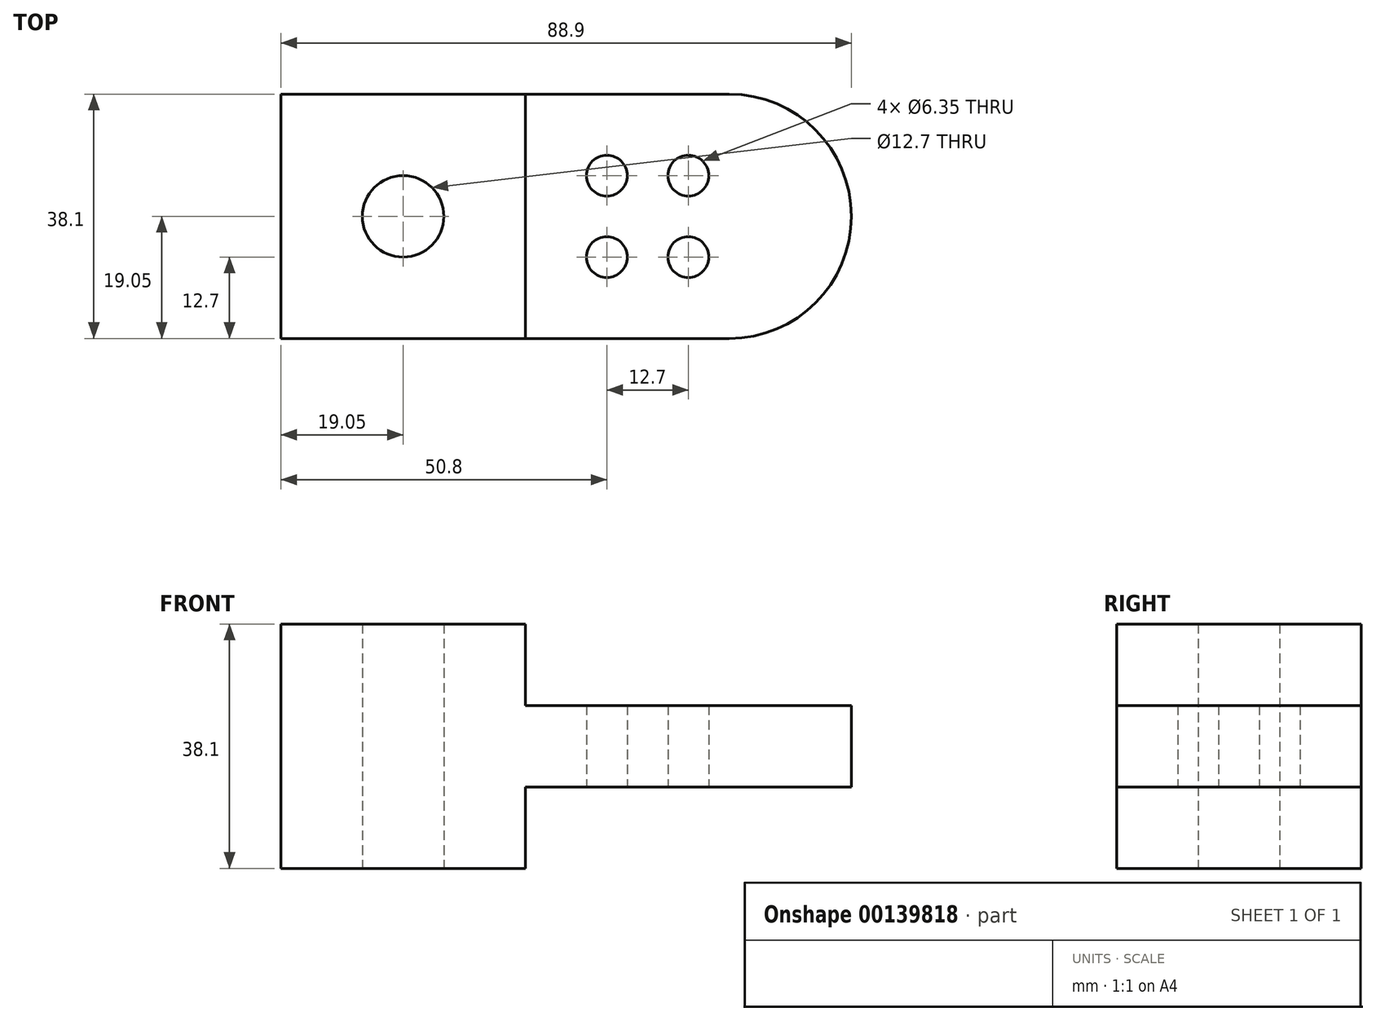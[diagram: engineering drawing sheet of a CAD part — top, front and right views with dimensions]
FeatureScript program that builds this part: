
annotation { "Feature Type Name" : "Feature", "Feature Type Description" : "" }
export const myFeature = defineFeature(function(context is Context, id is Id, definition is map)
    precondition{}
    {
        {
            var Q0;
            Q0=qCreatedBy(makeId("Top.planeOp"),FACE);
            var sketch = newSketch(context, id + "F0", { "sketchPlane" : qUnion([Q0])});
            skLineSegment(sketch, "E0.bottom", {"start": v(0, 0) * mm, "end": v(69.85, 0) * mm});
            skLineSegment(sketch, "E0.top", {"start": v(0, 38.1) * mm, "end": v(69.85, 38.1) * mm});
            skLineSegment(sketch, "E0.left", {"start": v(0, 0) * mm, "end": v(0, 38.1) * mm});
            skArc(sketch, "E1", {"start": v(69.85, 0) * mm, "mid": v(88.9, 19.05) * mm, "end": v(69.85, 38.1) * mm});
            skLineSegment(sketch, "E2", {"start": v(38.1, 38.1) * mm, "end": v(38.1, 0) * mm});
            skCircle(sketch, "E3", {"center": v(19.05, 19.05) * mm, "radius": 6.35 * mm});
            skCircle(sketch, "E4", {"center": v(50.8, 25.4) * mm, "radius": 3.18 * mm});
            skCircle(sketch, "E5", {"center": v(63.5, 25.4) * mm, "radius": 3.18 * mm});
            skCircle(sketch, "E6", {"center": v(50.8, 12.7) * mm, "radius": 3.18 * mm});
            skCircle(sketch, "E7", {"center": v(63.5, 12.7) * mm, "radius": 3.18 * mm});
            skSolve(sketch);
        }
        {
            var Q0;
            Q0 = qSketchRegion(id + "F0", true);
            extrude(context, id + "F1", {"entities" : qUnion([Q0]), "depth" : 12.7 * mm});
        }
        {
            var Q0;
            {var subQ1=sQuery(id+"F0.wireOp",EDGE,"E0.left");Q0=makeQuery(id+"F0.imprint","IMPRINT",FACE,{"disambiguationData":[TD([[makeQuery(id+"F0.imprint","IMPRINT",EDGE,{"derivedFrom":subQ1}),-1.0]])]});}
            extrude(context, id + "F2", {"entities" : qUnion([Q0]), "operationType" : NewBodyOperationType.ADD, "depth" : 25.4 * mm, "hasSecondDirection" : true, "secondDirectionOppositeDirection" : true, "secondDirectionDepth" : 12.7 * mm});
        }
    });
